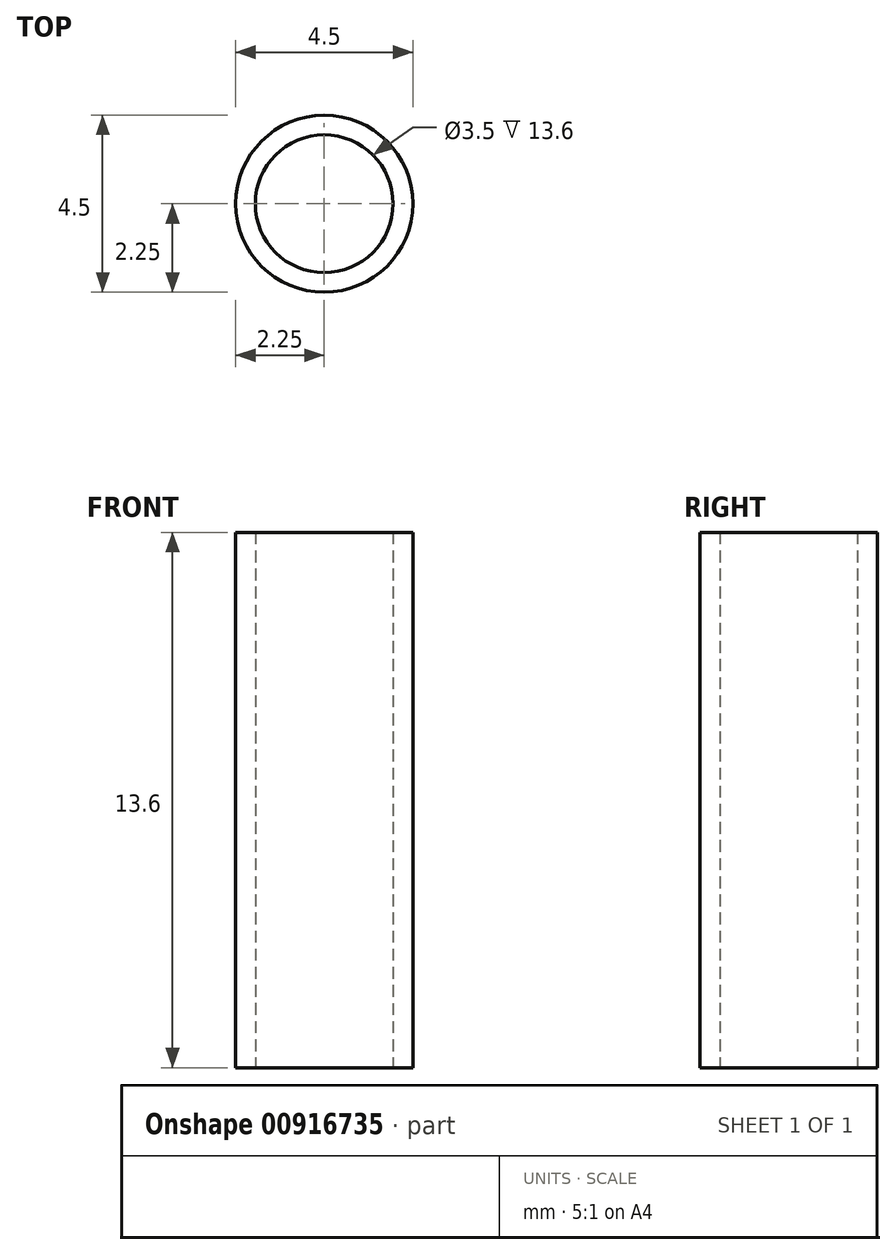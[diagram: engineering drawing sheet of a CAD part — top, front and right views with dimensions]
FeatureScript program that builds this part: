
annotation { "Feature Type Name" : "Feature", "Feature Type Description" : "" }
export const myFeature = defineFeature(function(context is Context, id is Id, definition is map)
    precondition{}
    {
        {
            assignVariable(context, id + "F0", {"name" : "spacing", "anyValue" : 13.6});
        }
        {
            var Q0;
            Q0=qCreatedBy(makeId("Top.planeOp"),FACE);
            var sketch = newSketch(context, id + "F1", { "sketchPlane" : qUnion([Q0])});
            skCircle(sketch, "E0", {"center": v(0, 0) * mm, "radius": 1.75 * mm});
            skCircle(sketch, "E1", {"center": v(0, 0) * mm, "radius": 2.25 * mm});
            skSolve(sketch);
        }
        {
            var Q0;
            Q0=makeQuery(id+"F1.imprint","IMPRINT",FACE,{"disambiguationData":[TD([[makeQuery(id+"F1.imprint","IMPRINT",EDGE,{"derivedFrom":sQuery(id+"F1.wireOp",EDGE,"E0")}),-1.0]])]});
            extrude(context, id + "F2", {"entities" : qUnion([Q0]), "depth" : (getVariable(context, 'spacing')) * mm, "offsetDistance" : 25 * mm});
        }
    });
